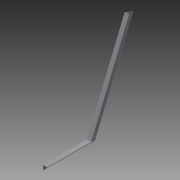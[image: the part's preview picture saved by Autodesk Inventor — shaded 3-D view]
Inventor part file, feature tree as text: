
AUTODESK INVENTOR PART (.ipt)
format: ipt  version: 2013 (Build 170138000, 138)  size: 113,152 bytes
history: native  units: in
note: dims shown in document units (in); Inventor stores cm internally (conversion verified against a paired STEP export)
features: extrude x2, sketch x2
ambient origin geometry x8: Origin, YZ Plane, XZ Plane, XY Plane, X Axis, Y Axis, Z Axis, Center Point
bodies: Solid1 (feature_tree)
feature tree (4):
  extrude  "Extrusion1"  TaperAngle=90.0deg  [1 undecoded]
  extrude  "Extrusion2"  TaperAngle=22.5deg  [1 undecoded]
  sketch  "Sketch1"  dims[d0=10.0in d1=90.0deg]
  sketch  "Sketch2"  dims[d2=22.5in d3=22.5deg d4=1.0in d5=180.0deg d6=2.0in d7=112.5deg d8=22.5in d9=90.0deg d12=90.0deg d17=0.5in d18=0.5in d19=0.5in d20=6.0in d22=0.5in d26=0.25in d27=0.25in d28=0.125in d29=0.0in d30=0.125in d31=22.5deg d33=0.125in d34=90.0deg d35=90.0deg d36=0.875in d37=0.0in]
note: 2 required parameter values undecoded (feature->parameter linkage not recoverable at this tier; creation-order binding heuristic only, values carry confidence <= 0.55)
